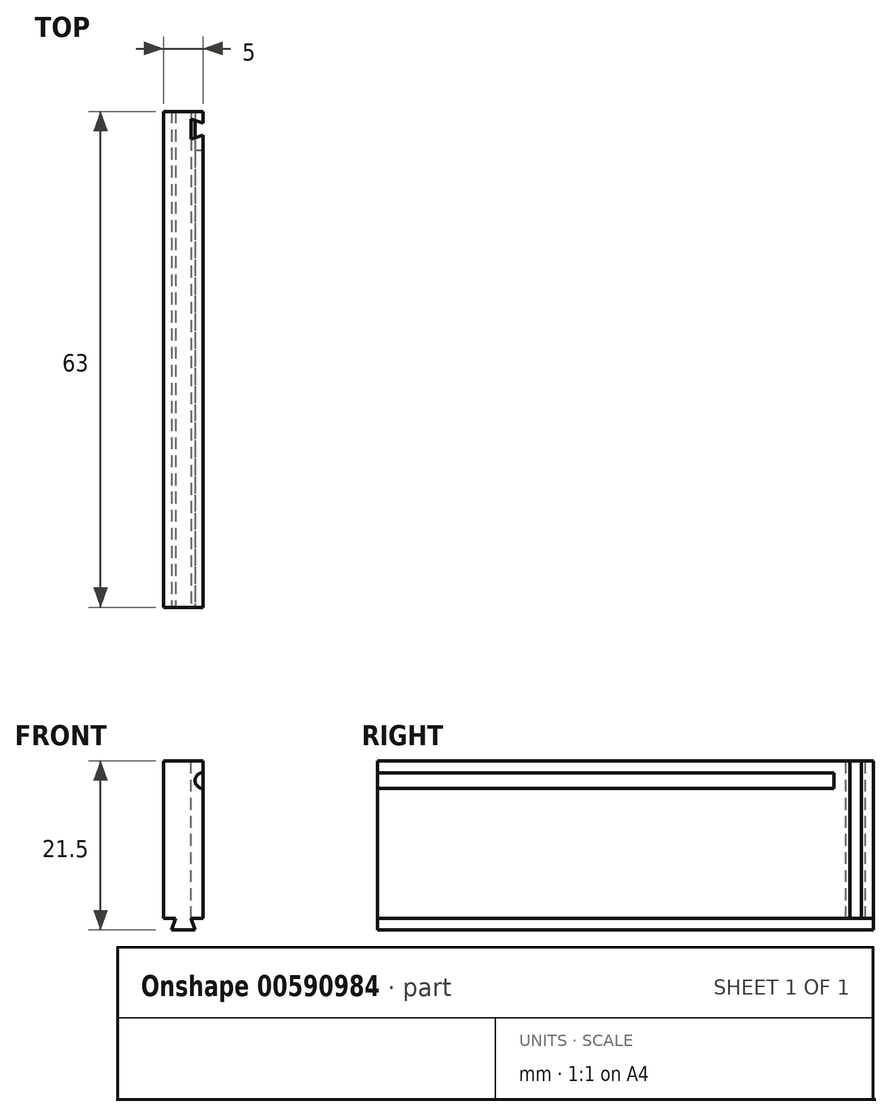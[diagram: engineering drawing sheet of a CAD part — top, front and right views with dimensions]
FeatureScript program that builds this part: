
annotation { "Feature Type Name" : "Feature", "Feature Type Description" : "" }
export const myFeature = defineFeature(function(context is Context, id is Id, definition is map)
    precondition{}
    {
        {
            var Q0;
            Q0=qCreatedBy(makeId("Right.planeOp"),FACE);
            var sketch = newSketch(context, id + "F0", { "sketchPlane" : qUnion([Q0])});
            skLineSegment(sketch, "E0.bottom", {"start": v(31.5, 10.75) * mm, "end": v(-31.5, 10.75) * mm});
            skLineSegment(sketch, "E0.top", {"start": v(31.5, -10.75) * mm, "end": v(-31.5, -10.75) * mm});
            skLineSegment(sketch, "E0.left", {"start": v(31.5, 10.75) * mm, "end": v(31.5, -10.75) * mm});
            skLineSegment(sketch, "E0.right", {"start": v(-31.5, 10.75) * mm, "end": v(-31.5, -10.75) * mm});
            skPoint(sketch, "E0.middle", {"position": v(0, 0) * mm});
            skSolve(sketch);
        }
        {
            var Q0;
            Q0=makeQuery(id+"F0.imprint","IMPRINT",FACE,{"disambiguationData":[TD([[makeQuery(id+"F0.imprint","IMPRINT",EDGE,{"derivedFrom":sQuery(id+"F0.wireOp",EDGE,"E0.bottom")}),1.0]])]});
            extrude(context, id + "F1", {"entities" : qUnion([Q0]), "depth" : 5 * mm, "offsetDistance" : 25 * mm});
        }
        {
            var Q0;
            Q0=makeQuery(id+"F1.opExtrude","SWEPT_FACE",FACE,{"disambiguationData":[OSD([sQuery(id+"F0.wireOp",EDGE,"E0.right")])]});
            var sketch = newSketch(context, id + "F2", { "sketchPlane" : qUnion([Q0])});
            skLineSegment(sketch, "E1", {"start": v(0, -9.25) * mm, "end": v(1.5, -9.25) * mm});
            skLineSegment(sketch, "E2", {"start": v(1.5, -9.25) * mm, "end": v(1, -10.75) * mm});
            skLineSegment(sketch, "E3", {"start": v(1, -10.75) * mm, "end": v(4, -10.75) * mm});
            skLineSegment(sketch, "E4", {"start": v(4, -10.75) * mm, "end": v(3.5, -9.25) * mm});
            skLineSegment(sketch, "E5", {"start": v(3.5, -9.25) * mm, "end": v(5, -9.25) * mm});
            skLineSegment(sketch, "E6", {"start": v(0, -9.25) * mm, "end": v(0, -10.75) * mm});
            skLineSegment(sketch, "E7", {"start": v(0, -10.75) * mm, "end": v(1, -10.75) * mm});
            skLineSegment(sketch, "E8", {"start": v(5, -9.25) * mm, "end": v(5, -10.75) * mm});
            skLineSegment(sketch, "E9", {"start": v(5, -10.75) * mm, "end": v(4, -10.75) * mm});
            skArc(sketch, "E10", {"start": v(5, 9.25) * mm, "mid": v(4, 8.25) * mm, "end": v(5, 7.25) * mm});
            skSolve(sketch);
        }
        {
            var Q0;
            {var subQ0=sQuery(id+"F2.wireOp",EDGE,"E10");Q0=makeQuery(id+"F2.imprint","IMPRINT",FACE,{"disambiguationData":[TD([[makeQuery(id+"F2.imprint","IMPRINT",EDGE,{"derivedFrom":subQ0}),1.0]])]});}
            extrude(context, id + "F3", {"entities" : qUnion([Q0]), "operationType" : NewBodyOperationType.REMOVE, "oppositeDirection" : true, "depth" : 58 * mm, "offsetDistance" : 25 * mm});
        }
        {
            var Q0;
            Q0=makeQuery(id+"F2.imprint","IMPRINT",FACE,{"disambiguationData":[TD([[makeQuery(id+"F2.imprint","IMPRINT",EDGE,{"derivedFrom":sQuery(id+"F2.wireOp",EDGE,"E1")}),-1.0]])]});
            var Q1;
            Q1=makeQuery(id+"F2.imprint","IMPRINT",FACE,{"disambiguationData":[TD([[makeQuery(id+"F2.imprint","IMPRINT",EDGE,{"derivedFrom":sQuery(id+"F2.wireOp",EDGE,"E4")}),-1.0]])]});
            extrude(context, id + "F4", {"entities" : qUnion([Q0, Q1]), "operationType" : NewBodyOperationType.REMOVE, "endBound" : BoundingType.THROUGH_ALL, "oppositeDirection" : true, "depth" : 25 * mm, "offsetDistance" : 25 * mm});
        }
        {
            var Q0;
            Q0=makeQuery(id+"F1.opExtrude","SWEPT_FACE",FACE,{"disambiguationData":[OSD([sQuery(id+"F0.wireOp",EDGE,"E0.bottom")])]});
            var sketch = newSketch(context, id + "F5", { "sketchPlane" : qUnion([Q0])});
            skLineSegment(sketch, "E11", {"start": v(5, 30) * mm, "end": v(3.5, 30.5) * mm});
            skLineSegment(sketch, "E12", {"start": v(3.5, 30.5) * mm, "end": v(3.5, 28) * mm});
            skLineSegment(sketch, "E13", {"start": v(3.5, 28) * mm, "end": v(5, 28.5) * mm});
            skLineSegment(sketch, "E14", {"start": v(5, 28.5) * mm, "end": v(5, 30) * mm});
            skSolve(sketch);
        }
        {
            var Q0;
            Q0=makeQuery(id+"F5.imprint","IMPRINT",FACE,{"disambiguationData":[TD([[makeQuery(id+"F5.imprint","IMPRINT",EDGE,{"derivedFrom":sQuery(id+"F5.wireOp",EDGE,"E11")}),1.0]])]});
            var Q1;
            Q1=makeQuery(id+"F4.boolean.opBoolean","COPY",FACE,{"derivedFrom":makeQuery(id+"F4.opExtrude","SWEPT_FACE",FACE,{"disambiguationData":[OSD([sQuery(id+"F2.wireOp",EDGE,"E5")])]})});
            extrude(context, id + "F6", {"entities" : qUnion([Q0]), "operationType" : NewBodyOperationType.REMOVE, "endBound" : BoundingType.UP_TO_SURFACE, "oppositeDirection" : true, "depth" : 20 * mm, "endBoundEntityFace" : qUnion([Q1]), "offsetDistance" : 25 * mm});
        }
    });
